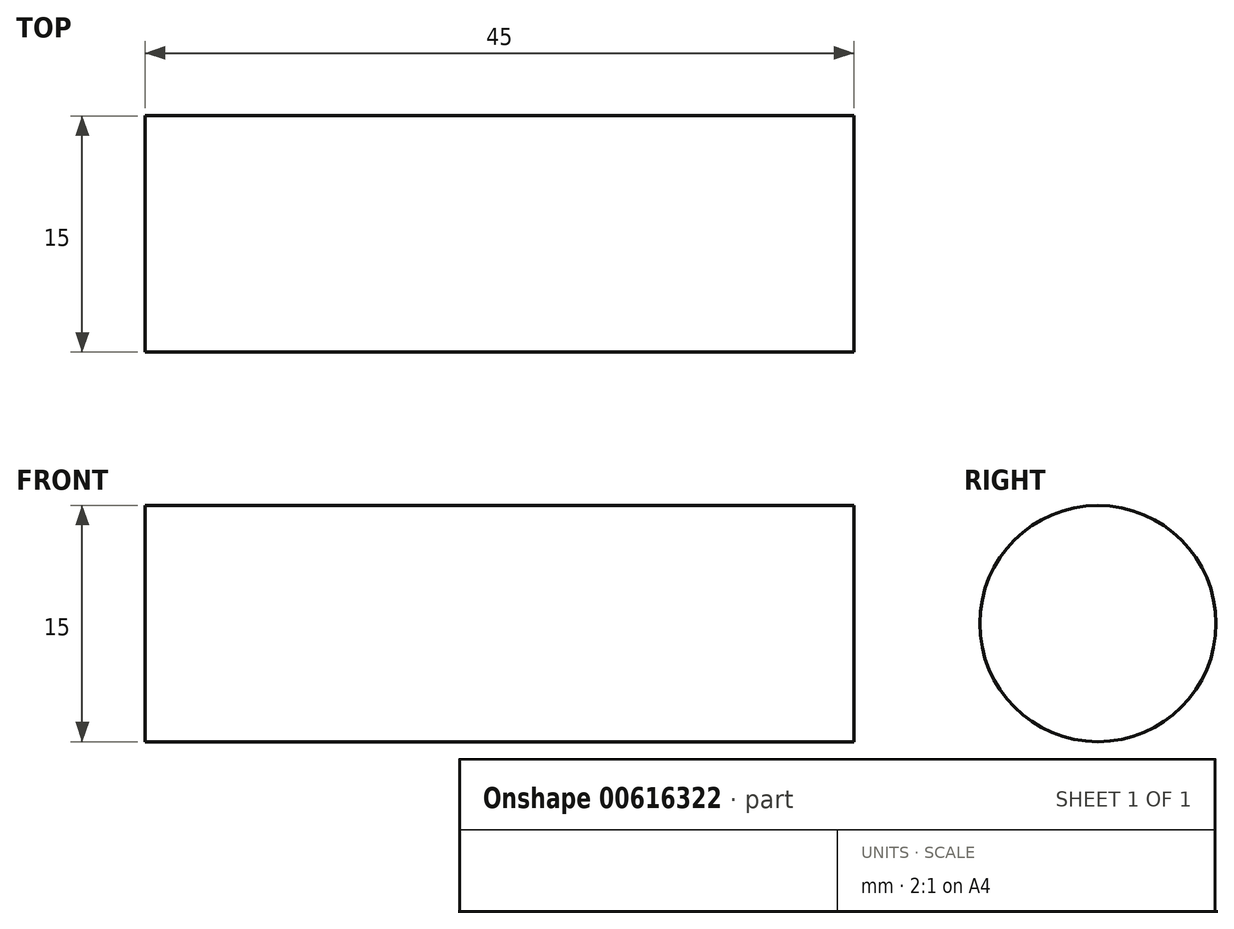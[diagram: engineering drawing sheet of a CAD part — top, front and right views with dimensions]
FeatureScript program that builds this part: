
annotation { "Feature Type Name" : "Feature", "Feature Type Description" : "" }
export const myFeature = defineFeature(function(context is Context, id is Id, definition is map)
    precondition{}
    {
        {
            var Q0;
            Q0=qCreatedBy(makeId("Right.planeOp"),FACE);
            var sketch = newSketch(context, id + "F0", { "sketchPlane" : qUnion([Q0])});
            skCircle(sketch, "E0", {"center": v(2.7, 0) * mm, "radius": 7.5 * mm});
            skSolve(sketch);
        }
        {
            var Q0;
            Q0 = qSketchRegion(id + "F0", true);
            extrude(context, id + "F1", {"entities" : qUnion([Q0]), "depth" : 45 * mm, "offsetDistance" : 25 * mm});
        }
    });
